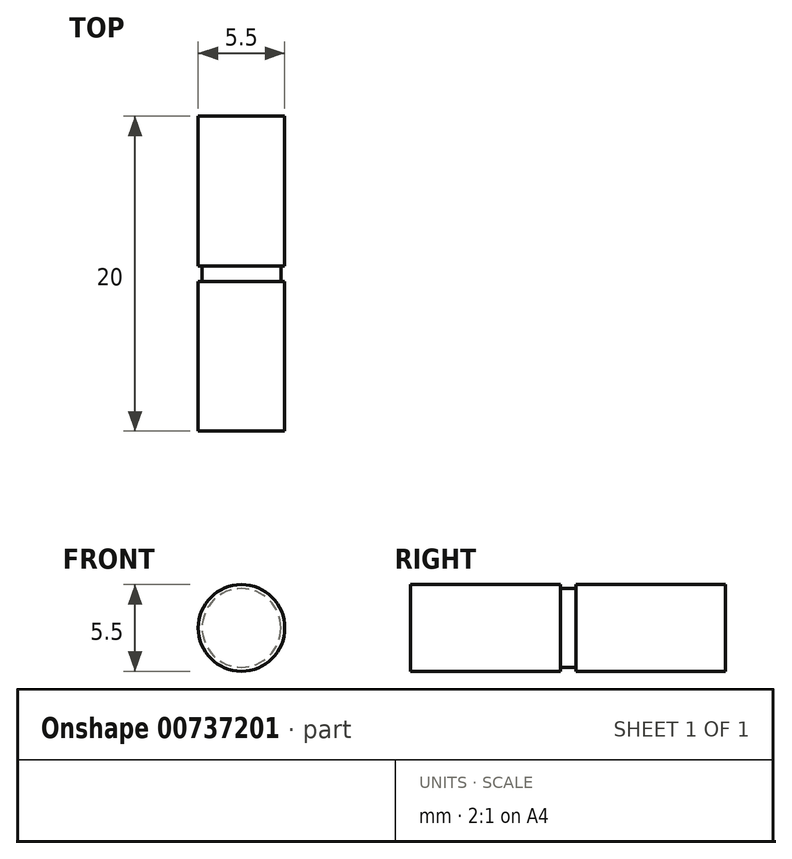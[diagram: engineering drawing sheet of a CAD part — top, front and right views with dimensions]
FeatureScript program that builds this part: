
annotation { "Feature Type Name" : "Feature", "Feature Type Description" : "" }
export const myFeature = defineFeature(function(context is Context, id is Id, definition is map)
    precondition{}
    {
        {
            var Q0;
            Q0=qCreatedBy(makeId("Front.planeOp"),FACE);
            var sketch = newSketch(context, id + "F0", { "sketchPlane" : qUnion([Q0])});
            skCircle(sketch, "E0", {"center": v(0, 0) * mm, "radius": 2.5 * mm});
            skSolve(sketch);
        }
        {
            var Q0;
            Q0=makeQuery(id+"F0.imprint","IMPRINT",FACE,{"disambiguationData":[TD([[makeQuery(id+"F0.imprint","IMPRINT",EDGE,{"derivedFrom":sQuery(id+"F0.wireOp",EDGE,"E0")}),1.0]])]});
            extrude(context, id + "F1", {"entities" : qUnion([Q0]), "depth" : 1 * mm, "offsetDistance" : 25 * mm});
        }
        {
            var Q0;
            Q0=makeQuery(id+"F1.opExtrude","CAP_FACE",FACE,{"disambiguationData":[OSD([sQuery(id+"F0.wireOp",EDGE,"E0")])],"isStart":true});
            var sketch = newSketch(context, id + "F2", { "sketchPlane" : qUnion([Q0])});
            skCircle(sketch, "E1", {"center": v(0, 0) * mm, "radius": 2.75 * mm});
            skSolve(sketch);
        }
        {
            var Q0;
            Q0 = qSketchRegion(id + "F2", true);
            extrude(context, id + "F3", {"entities" : qUnion([Q0]), "operationType" : NewBodyOperationType.ADD, "depth" : 9.5 * mm, "offsetDistance" : 25 * mm});
        }
        {
            var Q0;
            Q0=makeQuery(id+"F1.opExtrude","CAP_FACE",FACE,{"disambiguationData":[OSD([sQuery(id+"F0.wireOp",EDGE,"E0")])],"isStart":false});
            var sketch = newSketch(context, id + "F4", { "sketchPlane" : qUnion([Q0])});
            skCircle(sketch, "E2", {"center": v(0, 0) * mm, "radius": 2.75 * mm});
            skSolve(sketch);
        }
        {
            var Q0;
            Q0 = qSketchRegion(id + "F4", true);
            extrude(context, id + "F5", {"entities" : qUnion([Q0]), "operationType" : NewBodyOperationType.ADD, "depth" : 9.5 * mm, "offsetDistance" : 25 * mm});
        }
    });
